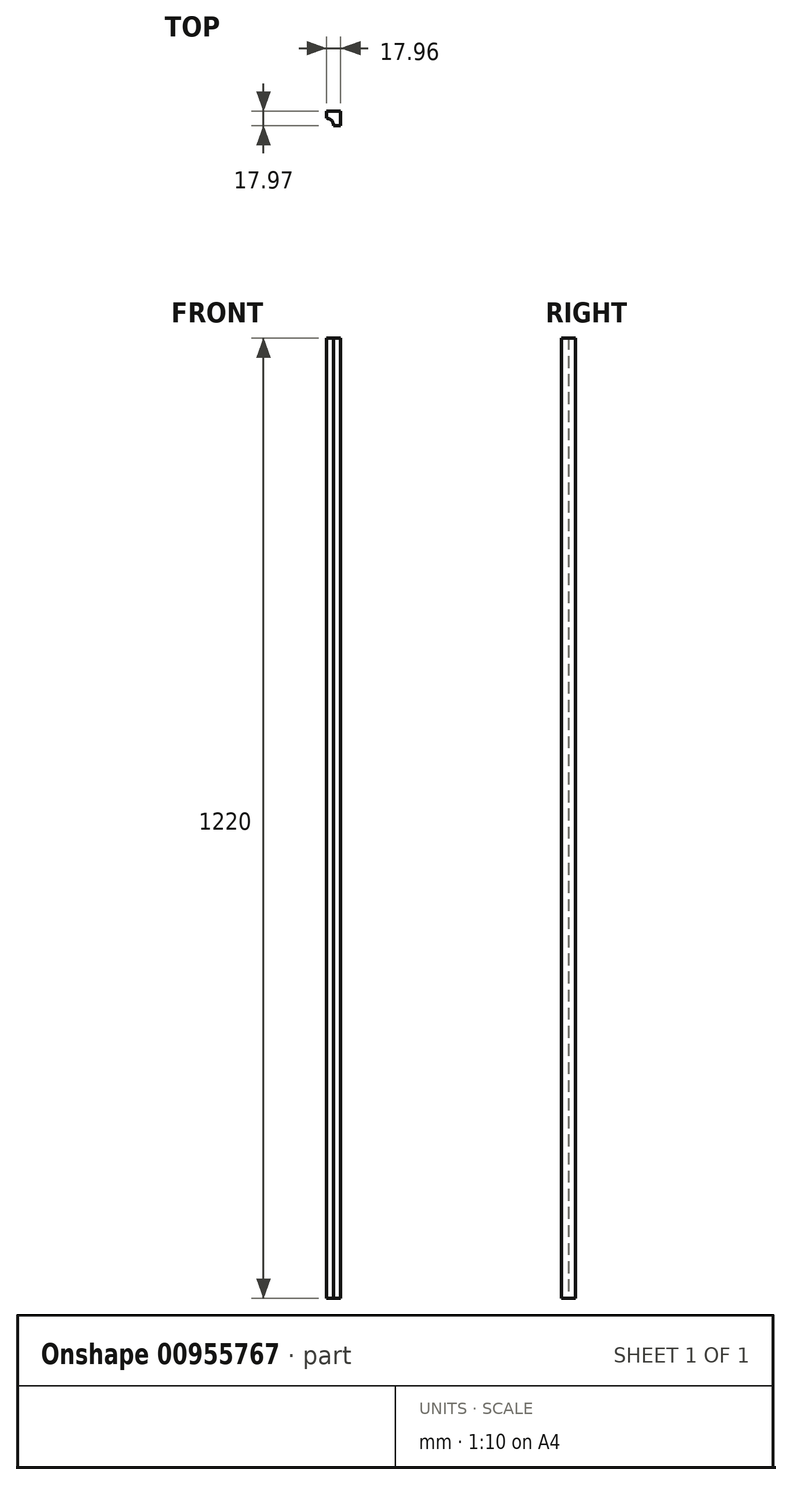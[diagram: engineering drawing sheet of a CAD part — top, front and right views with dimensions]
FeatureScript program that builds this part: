
annotation { "Feature Type Name" : "Feature", "Feature Type Description" : "" }
export const myFeature = defineFeature(function(context is Context, id is Id, definition is map)
    precondition{}
    {
        {
            var Q0;
            Q0=qCreatedBy(makeId("Top.planeOp"),FACE);
            var sketch = newSketch(context, id + "F0", { "sketchPlane" : qUnion([Q0])});
            skLineSegment(sketch, "E0.bottom", {"start": v(-35.23, -28.1) * mm, "end": v(-53.19, -28.1) * mm});
            skLineSegment(sketch, "E0.top", {"start": v(-35.23, -10.13) * mm, "end": v(-53.19, -10.13) * mm});
            skLineSegment(sketch, "E0.left", {"start": v(-35.23, -28.1) * mm, "end": v(-35.23, -10.13) * mm});
            skLineSegment(sketch, "E0.right", {"start": v(-53.19, -28.1) * mm, "end": v(-53.19, -10.13) * mm});
            skPoint(sketch, "E0.middle", {"position": v(-44.2, -19.11) * mm});
            skLineSegment(sketch, "E1", {"start": v(-44.2, -19.11) * mm, "end": v(-53.19, -19.11) * mm});
            skCircle(sketch, "E2", {"center": v(-53.19, -28.1) * mm, "radius": 8.98 * mm});
            skSolve(sketch);
        }
        {
            var Q0;
            {var subQ1=sQuery(id+"F0.wireOp",EDGE,"E0.top");Q0=makeQuery(id+"F0.imprint","IMPRINT",FACE,{"disambiguationData":[TD([[makeQuery(id+"F0.imprint","IMPRINT",EDGE,{"derivedFrom":subQ1}),1.0]])]});}
            extrude(context, id + "F1", {"entities" : qUnion([Q0]), "depth" : 1220 * mm, "offsetDistance" : 25.4 * mm});
        }
    });
